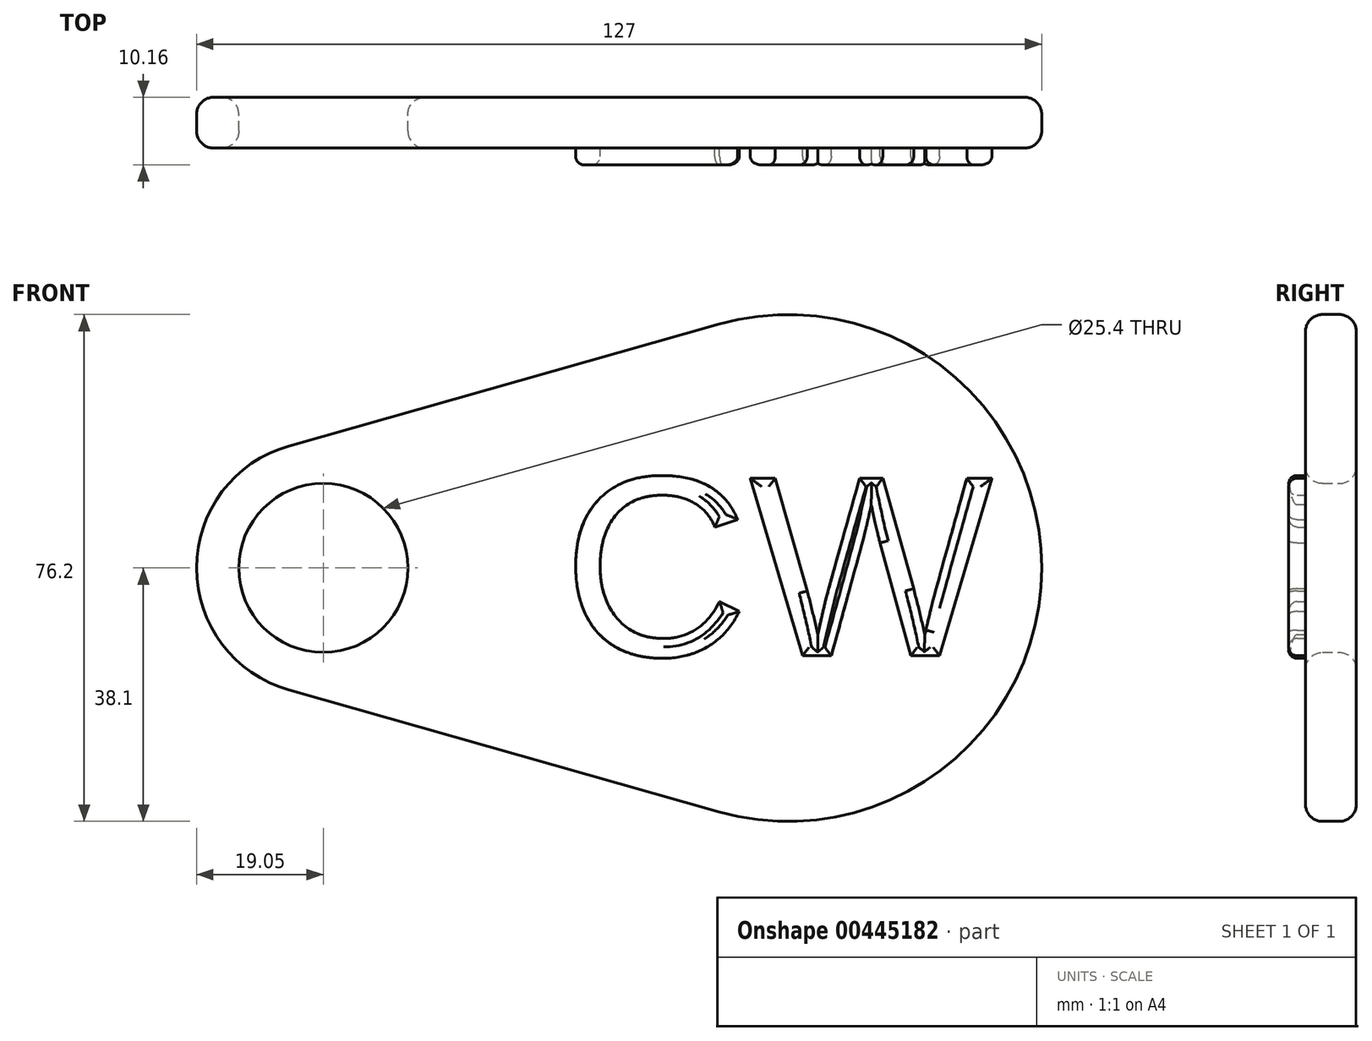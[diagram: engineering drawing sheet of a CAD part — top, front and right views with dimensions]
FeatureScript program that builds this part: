
annotation { "Feature Type Name" : "Feature", "Feature Type Description" : "" }
export const myFeature = defineFeature(function(context is Context, id is Id, definition is map)
    precondition{}
    {
        {
            var Q0;
            Q0=qCreatedBy(makeId("Front.planeOp"),FACE);
            var sketch = newSketch(context, id + "F0", { "sketchPlane" : qUnion([Q0])});
            skCircle(sketch, "E0", {"center": v(0, 0) * mm, "radius": 38.1 * mm});
            skCircle(sketch, "E1", {"center": v(-69.85, 0) * mm, "radius": 19.05 * mm});
            skLineSegment(sketch, "E2", {"start": v(-75.05, 18.33) * mm, "end": v(-10.4, 36.66) * mm});
            skLineSegment(sketch, "E3", {"start": v(-10.4, -36.66) * mm, "end": v(-75.05, -18.33) * mm});
            skCircle(sketch, "E4", {"center": v(-69.85, 0) * mm, "radius": 12.7 * mm});
            skSolve(sketch);
        }
        {
            var Q0;
            Q0 = qSketchRegion(id + "F0", true);
            extrude(context, id + "F1", {"entities" : qUnion([Q0]), "depth" : 7.62 * mm});
        }
        {
            var Q0;
            Q0=makeQuery(id+"F1.opExtrude","CAP_EDGE",EDGE,{"disambiguationData":[OSD([sQuery(id+"F0.wireOp",EDGE,"E2")])],"isStart":false});
            var Q1;
            Q1=makeQuery(id+"F1.opExtrude","CAP_EDGE",EDGE,{"disambiguationData":[OSD([sQuery(id+"F0.wireOp",EDGE,"E1")])],"isStart":false});
            var Q2;
            Q2=makeQuery(id+"F1.opExtrude","CAP_EDGE",EDGE,{"disambiguationData":[OSD([sQuery(id+"F0.wireOp",EDGE,"E4")])],"isStart":false});
            var Q3;
            Q3=makeQuery(id+"F1.opExtrude","CAP_EDGE",EDGE,{"disambiguationData":[OSD([sQuery(id+"F0.wireOp",EDGE,"E3")])],"isStart":false});
            var Q4;
            Q4=makeQuery(id+"F1.opExtrude","CAP_EDGE",EDGE,{"disambiguationData":[OSD([sQuery(id+"F0.wireOp",EDGE,"E0")])],"isStart":false});
            fillet(context, id + "F2", {"entities" : qUnion([Q0, Q1, Q2, Q3, Q4]), "radius" : 2.54 * mm, "tangentPropagation" : true, "allowEdgeOverflow" : false});
        }
        {
            var Q0;
            Q0=makeQuery(id+"F1.opExtrude","CAP_EDGE",EDGE,{"disambiguationData":[OSD([sQuery(id+"F0.wireOp",EDGE,"E0")])],"isStart":true});
            var Q1;
            Q1=makeQuery(id+"F1.opExtrude","CAP_EDGE",EDGE,{"disambiguationData":[OSD([sQuery(id+"F0.wireOp",EDGE,"E3")])],"isStart":true});
            var Q2;
            Q2=makeQuery(id+"F1.opExtrude","CAP_EDGE",EDGE,{"disambiguationData":[OSD([sQuery(id+"F0.wireOp",EDGE,"E1")])],"isStart":true});
            var Q3;
            Q3=makeQuery(id+"F1.opExtrude","CAP_EDGE",EDGE,{"disambiguationData":[OSD([sQuery(id+"F0.wireOp",EDGE,"E4")])],"isStart":true});
            var Q4;
            Q4=makeQuery(id+"F1.opExtrude","CAP_EDGE",EDGE,{"disambiguationData":[OSD([sQuery(id+"F0.wireOp",EDGE,"E2")])],"isStart":true});
            fillet(context, id + "F3", {"entities" : qUnion([Q0, Q1, Q2, Q3, Q4]), "radius" : 2.54 * mm, "tangentPropagation" : true, "allowEdgeOverflow" : false});
        }
        {
            var Q0;
            Q0=makeQuery(id+"F1.opExtrude","CAP_FACE",FACE,{"disambiguationData":[OSD([sQuery(id+"F0.wireOp",EDGE,"E0"),sQuery(id+"F0.wireOp",EDGE,"E1"),sQuery(id+"F0.wireOp",EDGE,"E2"),sQuery(id+"F0.wireOp",EDGE,"E3"),sQuery(id+"F0.wireOp",EDGE,"E4")])],"isStart":false});
            var sketch = newSketch(context, id + "F4", { "sketchPlane" : qUnion([Q0])});
            skText(sketch, "E5", { "text": "CW\n", "fontName": "Arimo-Regular.ttf"});
            const initialGuessF4  = {"E5": [-0.0339, -0.0132, 1, 0, 0.02794]};
            skSetInitialGuess(sketch, initialGuessF4);
            skSolve(sketch);
        }
        {
            var Q0;
            Q0 = qSketchRegion(id + "F4", true);
            extrude(context, id + "F5", {"entities" : qUnion([Q0]), "operationType" : NewBodyOperationType.ADD, "depth" : 2.54 * mm});
        }
        {
            var Q0;
            Q0=makeQuery(id+"F5.opExtrude","CAP_FACE",FACE,{"disambiguationData":[OSD([sQuery(id+"F4.wireOp",EDGE,"E5.sketch_text.stroke-0"),sQuery(id+"F4.wireOp",EDGE,"E5.sketch_text.stroke-1"),sQuery(id+"F4.wireOp",EDGE,"E5.sketch_text.stroke-2"),sQuery(id+"F4.wireOp",EDGE,"E5.sketch_text.stroke-3"),sQuery(id+"F4.wireOp",EDGE,"E5.sketch_text.stroke-4"),sQuery(id+"F4.wireOp",EDGE,"E5.sketch_text.stroke-5"),sQuery(id+"F4.wireOp",EDGE,"E5.sketch_text.stroke-6"),sQuery(id+"F4.wireOp",EDGE,"E5.sketch_text.stroke-7"),sQuery(id+"F4.wireOp",EDGE,"E5.sketch_text.stroke-8"),sQuery(id+"F4.wireOp",EDGE,"E5.sketch_text.stroke-9"),sQuery(id+"F4.wireOp",EDGE,"E5.sketch_text.stroke-10"),sQuery(id+"F4.wireOp",EDGE,"E5.sketch_text.stroke-11"),sQuery(id+"F4.wireOp",EDGE,"E5.sketch_text.stroke-12"),sQuery(id+"F4.wireOp",EDGE,"E5.sketch_text.stroke-13"),sQuery(id+"F4.wireOp",EDGE,"E5.sketch_text.stroke-14"),sQuery(id+"F4.wireOp",EDGE,"E5.sketch_text.stroke-15"),sQuery(id+"F4.wireOp",EDGE,"E5.sketch_text.stroke-16"),sQuery(id+"F4.wireOp",EDGE,"E5.sketch_text.stroke-17")])],"isStart":false});
            var Q1;
            Q1=makeQuery(id+"F5.opExtrude","CAP_FACE",FACE,{"disambiguationData":[OSD([sQuery(id+"F4.wireOp",EDGE,"E5.sketch_text.stroke-18"),sQuery(id+"F4.wireOp",EDGE,"E5.sketch_text.stroke-19"),sQuery(id+"F4.wireOp",EDGE,"E5.sketch_text.stroke-20"),sQuery(id+"F4.wireOp",EDGE,"E5.sketch_text.stroke-21"),sQuery(id+"F4.wireOp",EDGE,"E5.sketch_text.stroke-22"),sQuery(id+"F4.wireOp",EDGE,"E5.sketch_text.stroke-23"),sQuery(id+"F4.wireOp",EDGE,"E5.sketch_text.stroke-24"),sQuery(id+"F4.wireOp",EDGE,"E5.sketch_text.stroke-25"),sQuery(id+"F4.wireOp",EDGE,"E5.sketch_text.stroke-26"),sQuery(id+"F4.wireOp",EDGE,"E5.sketch_text.stroke-27"),sQuery(id+"F4.wireOp",EDGE,"E5.sketch_text.stroke-28"),sQuery(id+"F4.wireOp",EDGE,"E5.sketch_text.stroke-29"),sQuery(id+"F4.wireOp",EDGE,"E5.sketch_text.stroke-30"),sQuery(id+"F4.wireOp",EDGE,"E5.sketch_text.stroke-31"),sQuery(id+"F4.wireOp",EDGE,"E5.sketch_text.stroke-32"),sQuery(id+"F4.wireOp",EDGE,"E5.sketch_text.stroke-33"),sQuery(id+"F4.wireOp",EDGE,"E5.sketch_text.stroke-34"),sQuery(id+"F4.wireOp",EDGE,"E5.sketch_text.stroke-35"),sQuery(id+"F4.wireOp",EDGE,"E5.sketch_text.stroke-36"),sQuery(id+"F4.wireOp",EDGE,"E5.sketch_text.stroke-37")])],"isStart":false});
            fillet(context, id + "F6", {"entities" : qUnion([Q0, Q1]), "radius" : 1.27 * mm, "tangentPropagation" : true, "allowEdgeOverflow" : false});
        }
    });
